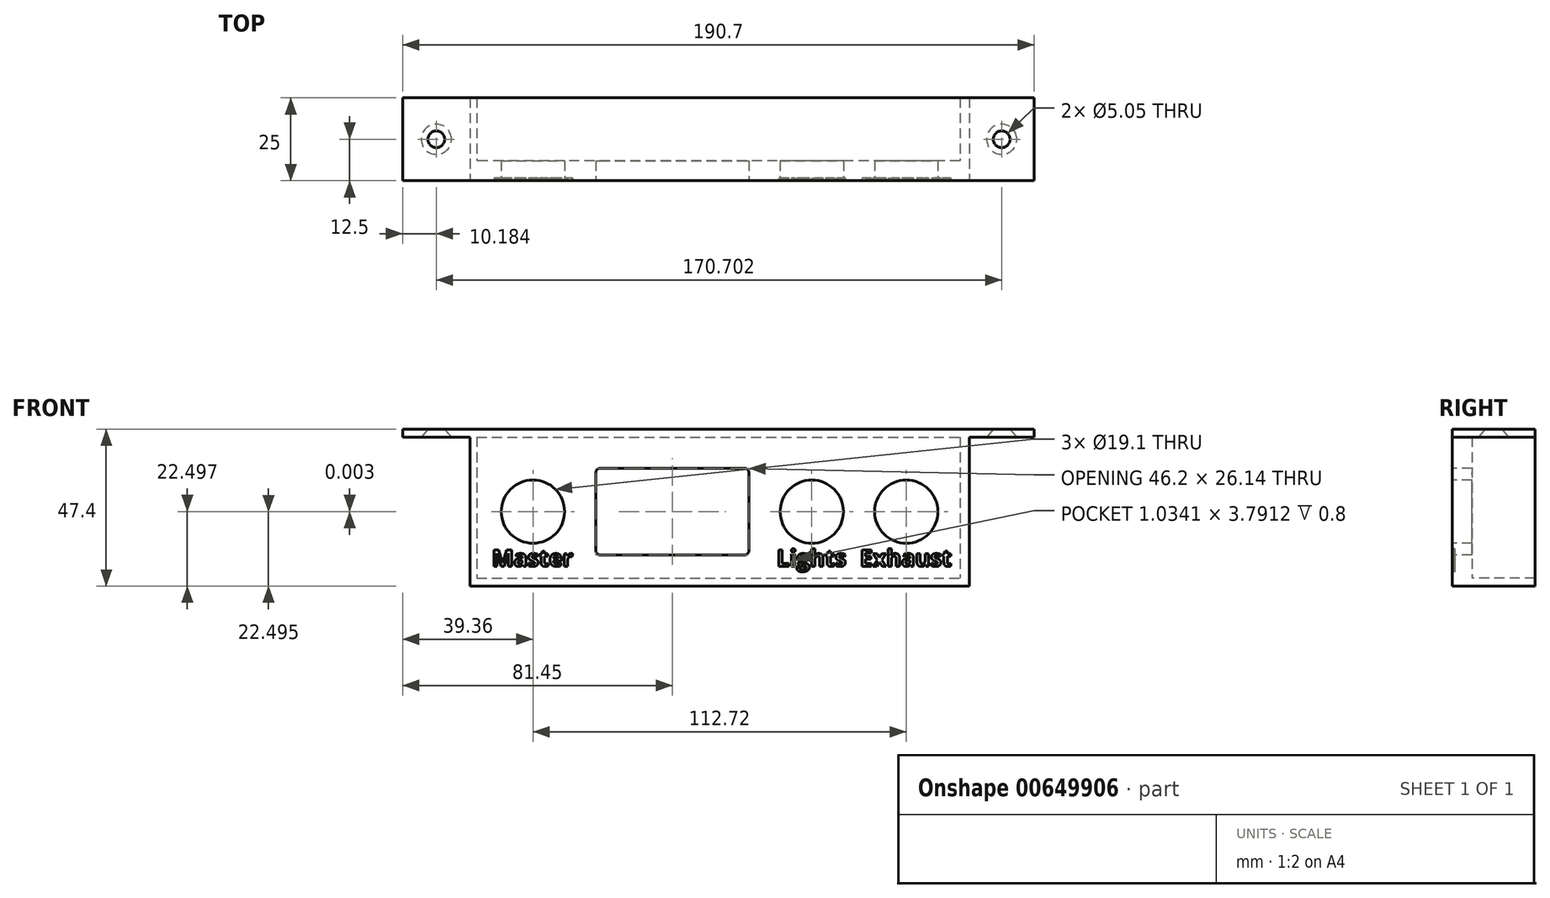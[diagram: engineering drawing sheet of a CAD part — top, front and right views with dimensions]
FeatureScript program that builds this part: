
annotation { "Feature Type Name" : "Feature", "Feature Type Description" : "" }
export const myFeature = defineFeature(function(context is Context, id is Id, definition is map)
    precondition{}
    {
        {
            var Q0;
            Q0=qCreatedBy(makeId("Front.planeOp"),FACE);
            var sketch = newSketch(context, id + "F0", { "sketchPlane" : qUnion([Q0])});
            skCircle(sketch, "E0", {"center": v(56.73, 0) * mm, "radius": 9.55 * mm});
            skCircle(sketch, "E1", {"center": v(28.2, 0) * mm, "radius": 9.55 * mm});
            skCircle(sketch, "E2", {"center": v(-55.99, 0) * mm, "radius": 9.55 * mm});
            skLineSegment(sketch, "E3.bottom", {"start": v(-35.73, -13.07) * mm, "end": v(7.93, -13.07) * mm});
            skLineSegment(sketch, "E3.top", {"start": v(-35.73, 13.07) * mm, "end": v(7.93, 13.07) * mm});
            skLineSegment(sketch, "E3.left", {"start": v(-37, -11.8) * mm, "end": v(-37, 11.8) * mm});
            skLineSegment(sketch, "E3.right", {"start": v(9.2, -11.8) * mm, "end": v(9.2, 11.8) * mm});
            skPoint(sketch, "E3.middle", {"position": v(-13.9, 0) * mm});
            skPoint(sketch, "E4.visualSharp", {"position": v(-37, -13.07) * mm});
            skArc(sketch, "E4.filletArc", {"start": v(-37, -11.8) * mm, "mid": v(-36.63, -12.7) * mm, "end": v(-35.73, -13.07) * mm});
            skPoint(sketch, "E5.visualSharp", {"position": v(9.2, -13.07) * mm});
            skArc(sketch, "E5.filletArc", {"start": v(7.93, -13.07) * mm, "mid": v(8.83, -12.7) * mm, "end": v(9.2, -11.8) * mm});
            skPoint(sketch, "E6.visualSharp", {"position": v(9.2, 13.07) * mm});
            skArc(sketch, "E6.filletArc", {"start": v(9.2, 11.8) * mm, "mid": v(8.83, 12.7) * mm, "end": v(7.93, 13.07) * mm});
            skPoint(sketch, "E7.visualSharp", {"position": v(-37, 13.07) * mm});
            skArc(sketch, "E7.filletArc", {"start": v(-35.73, 13.07) * mm, "mid": v(-36.63, 12.7) * mm, "end": v(-37, 11.8) * mm});
            skLineSegment(sketch, "E8.top", {"start": v(-74.98, -22.5) * mm, "end": v(75.72, -22.5) * mm});
            skLineSegment(sketch, "E8.left", {"start": v(-74.98, 22.5) * mm, "end": v(-74.98, -22.5) * mm});
            skLineSegment(sketch, "E8.right", {"start": v(75.72, 22.5) * mm, "end": v(75.72, -22.5) * mm});
            skPoint(sketch, "E9", {"position": v(0, 0) * mm});
            skLineSegment(sketch, "E10.bottom", {"start": v(-95.35, 24.9) * mm, "end": v(95.35, 24.9) * mm});
            skLineSegment(sketch, "E10.top", {"start": v(-95.35, 22.5) * mm, "end": v(-74.98, 22.5) * mm});
            skLineSegment(sketch, "E10.left", {"start": v(-95.35, 24.9) * mm, "end": v(-95.35, 22.5) * mm});
            skLineSegment(sketch, "E10.right", {"start": v(95.35, 24.9) * mm, "end": v(95.35, 22.5) * mm});
            skPoint(sketch, "E10.middle", {"position": v(0, 23.7) * mm});
            skLineSegment(sketch, "E11.trimOffspring", {"start": v(75.72, 22.5) * mm, "end": v(95.35, 22.5) * mm});
            skLineSegment(sketch, "E12.bottom", {"start": v(95.35, 22.5) * mm, "end": v(-95.35, 22.5) * mm});
            skLineSegment(sketch, "E12.top", {"start": v(95.35, 24.9) * mm, "end": v(-95.35, 24.9) * mm});
            skLineSegment(sketch, "E12.left", {"start": v(95.35, 22.5) * mm, "end": v(95.35, 24.9) * mm});
            skLineSegment(sketch, "E12.right", {"start": v(-95.35, 22.5) * mm, "end": v(-95.35, 24.9) * mm});
            skSolve(sketch);
        }
        {
            var Q0;
            Q0=makeQuery(id+"F0.imprint","IMPRINT",FACE,{"disambiguationData":[TD([[makeQuery(id+"F0.imprint","IMPRINT",EDGE,{"derivedFrom":sQuery(id+"F0.wireOp",EDGE,"E0")}),-1.0]])]});
            extrude(context, id + "F1", {"entities" : qUnion([Q0]), "oppositeDirection" : true, "depth" : 6 * mm, "offsetDistance" : 25 * mm});
        }
        {
            var Q0;
            Q0=makeQuery(id+"F0.imprint","IMPRINT",FACE,{"disambiguationData":[TD([[makeQuery(id+"F0.imprint","IMPRINT",EDGE,{"derivedFrom":sQuery(id+"F0.wireOp",EDGE,"E10.bottom")}),-1.0]])]});
            extrude(context, id + "F2", {"entities" : qUnion([Q0]), "operationType" : NewBodyOperationType.ADD, "oppositeDirection" : true, "depth" : 25 * mm, "offsetDistance" : 25 * mm});
        }
        {
            var Q0;
            Q0=qCreatedBy(makeId("Front.planeOp"),FACE);
            var sketch = newSketch(context, id + "F3", { "sketchPlane" : qUnion([Q0])});
            skLineSegment(sketch, "E13.0", {"start": v(-74.98, -22.5) * mm, "end": v(75.72, -22.5) * mm});
            skLineSegment(sketch, "E13.1", {"start": v(75.72, 22.5) * mm, "end": v(75.72, -22.5) * mm});
            skLineSegment(sketch, "E13.2", {"start": v(-74.98, 22.5) * mm, "end": v(-74.98, -22.5) * mm});
            skLineSegment(sketch, "E13.3", {"start": v(95.35, 22.5) * mm, "end": v(72.95, 22.5) * mm});
            skLineSegment(sketch, "E14.left", {"start": v(72.95, 20.1) * mm, "end": v(72.95, -20.1) * mm});
            skLineSegment(sketch, "E14.right", {"start": v(-72.95, 20.1) * mm, "end": v(-72.95, -20.1) * mm});
            skPoint(sketch, "E14.middle", {"position": v(0, 0) * mm});
            skLineSegment(sketch, "E15", {"start": v(-72.95, 22.5) * mm, "end": v(-72.95, -20.1) * mm});
            skLineSegment(sketch, "E16", {"start": v(72.95, 22.5) * mm, "end": v(72.95, -20.1) * mm});
            skLineSegment(sketch, "E17", {"start": v(-72.95, -20.1) * mm, "end": v(72.95, -20.1) * mm});
            skLineSegment(sketch, "E18.trimOffspring", {"start": v(-72.95, 22.5) * mm, "end": v(-95.35, 22.5) * mm});
            skSolve(sketch);
        }
        {
            var Q0;
            Q0=makeQuery(id+"F3.imprint","IMPRINT",FACE,{"disambiguationData":[TD([[makeQuery(id+"F3.imprint","IMPRINT",EDGE,{"derivedFrom":sQuery(id+"F3.wireOp",EDGE,"E13.0")}),1.0]])]});
            extrude(context, id + "F4", {"entities" : qUnion([Q0]), "operationType" : NewBodyOperationType.ADD, "oppositeDirection" : true, "depth" : 25 * mm, "offsetDistance" : 25 * mm});
        }
        {
            var Q0;
            {var subQ0=sQuery(id+"F0.wireOp",EDGE,"E12.bottom");var subQ1=sQuery(id+"F0.wireOp",EDGE,"E11.trimOffspring");var subQ4=sQuery(id+"F0.wireOp",EDGE,"E10.top");var subQ6=sQuery(id+"F0.wireOp",EDGE,"E8.right");Q0=makeQuery(id+"F4.boolean.opBoolean","SPLIT",FACE,{"disambiguationData":[TD([makeQuery(id+"F1.opExtrude","SWEPT_FACE",FACE,{"disambiguationData":[OSD([subQ6])]})])],"derivedFrom":makeQuery(id+"F2.opExtrude","SWEPT_FACE",FACE,{"disambiguationData":[OSD([subQ4,subQ1,subQ0])]})});}
            var sketch = newSketch(context, id + "F5", { "sketchPlane" : qUnion([Q0])});
            skLineSegment(sketch, "E19.0.0", {"start": v(75.72, 0) * mm, "end": v(75.72, -25) * mm});
            skLineSegment(sketch, "E19.0.1", {"start": v(75.72, -25) * mm, "end": v(95.35, -25) * mm});
            skLineSegment(sketch, "E19.0.2", {"start": v(95.35, -25) * mm, "end": v(95.35, 0) * mm});
            skLineSegment(sketch, "E19.0.3", {"start": v(95.35, 0) * mm, "end": v(75.72, 0) * mm});
            skLineSegment(sketch, "E20.0.0", {"start": v(-95.35, -25) * mm, "end": v(-74.98, -25) * mm});
            skLineSegment(sketch, "E20.0.1", {"start": v(-74.98, -25) * mm, "end": v(-74.98, 0) * mm});
            skLineSegment(sketch, "E20.0.2", {"start": v(-74.98, 0) * mm, "end": v(-95.35, 0) * mm});
            skLineSegment(sketch, "E20.0.3", {"start": v(-95.35, 0) * mm, "end": v(-95.35, -25) * mm});
            skPoint(sketch, "E21", {"position": v(85.54, -12.5) * mm});
            skPoint(sketch, "E21.positionSnap0", {"position": v(95.35, -12.5) * mm});
            skPoint(sketch, "E21.positionSnap1", {"position": v(85.54, -25) * mm});
            skPoint(sketch, "E22", {"position": v(-85.17, -12.5) * mm});
            skPoint(sketch, "E22.positionSnap0", {"position": v(-85.17, -25) * mm});
            skPoint(sketch, "E22.positionSnap1", {"position": v(-95.35, -12.5) * mm});
            skSolve(sketch);
        }
        {
            var Q0;
            Q0=sQuery(id+"F5.wireOp",VERTEX,"E21");
            var Q1;
            Q1=sQuery(id+"F5.wireOp",VERTEX,"E22");
            var Q2;
            Q2=makeQuery(id+"F1.opExtrude","SWEPT_BODY",BODY,{"disambiguationData":[OSD([sQuery(id+"F0.wireOp",EDGE,"E0"),sQuery(id+"F0.wireOp",EDGE,"E1"),sQuery(id+"F0.wireOp",EDGE,"E2"),sQuery(id+"F0.wireOp",EDGE,"E3.bottom"),sQuery(id+"F0.wireOp",EDGE,"E3.top"),sQuery(id+"F0.wireOp",EDGE,"E3.left"),sQuery(id+"F0.wireOp",EDGE,"E3.right"),sQuery(id+"F0.wireOp",EDGE,"E4.filletArc"),sQuery(id+"F0.wireOp",EDGE,"E5.filletArc"),sQuery(id+"F0.wireOp",EDGE,"E6.filletArc"),sQuery(id+"F0.wireOp",EDGE,"E7.filletArc"),sQuery(id+"F0.wireOp",EDGE,"E8.top"),sQuery(id+"F0.wireOp",EDGE,"E8.left"),sQuery(id+"F0.wireOp",EDGE,"E8.right"),sQuery(id+"F0.wireOp",EDGE,"E12.bottom")])]});
            hole(context, id + "F6", {"style" : HoleStyle.C_SINK, "endStyle" : HoleEndStyle.THROUGH, "standardTappedOrClearance" : lookupTablePath({ "standard" : "ANSI", "size" : "#8 (0.2)", "type" : "Drilled" }), "standardBlindInLast" : lookupTablePath({ "standard" : "ANSI", "size" : "#8", "type" : "Drilled" }), "holeDiameter" : 5.05 * mm, "cSinkDiameter" : 9.12 * mm, "cSinkAngle" : 82 * degree, "majorDiameter" : 4.17 * mm, "isTappedThrough" : true, "tappedDepth" : 12 * mm, "tapClearance" : 3, "locations" : qUnion([Q0, Q1]), "scope" : qUnion([Q2])});
        }
        {
            var Q0;
            {var subQ0=sQuery(id+"F0.wireOp",EDGE,"E12.bottom");Q0=makeQuery(id+"F2.boolean.opBoolean","MERGE",FACE,{"derivedFrom":[makeQuery(id+"F1.opExtrude","CAP_FACE",FACE,{"disambiguationData":[OSD([sQuery(id+"F0.wireOp",EDGE,"E0"),sQuery(id+"F0.wireOp",EDGE,"E1"),sQuery(id+"F0.wireOp",EDGE,"E2"),sQuery(id+"F0.wireOp",EDGE,"E3.bottom"),sQuery(id+"F0.wireOp",EDGE,"E3.top"),sQuery(id+"F0.wireOp",EDGE,"E3.left"),sQuery(id+"F0.wireOp",EDGE,"E3.right"),sQuery(id+"F0.wireOp",EDGE,"E4.filletArc"),sQuery(id+"F0.wireOp",EDGE,"E5.filletArc"),sQuery(id+"F0.wireOp",EDGE,"E6.filletArc"),sQuery(id+"F0.wireOp",EDGE,"E7.filletArc"),sQuery(id+"F0.wireOp",EDGE,"E8.top"),sQuery(id+"F0.wireOp",EDGE,"E8.left"),sQuery(id+"F0.wireOp",EDGE,"E8.right"),subQ0])],"isStart":true}),makeQuery(id+"F2.opExtrude","CAP_FACE",FACE,{"disambiguationData":[OSD([sQuery(id+"F0.wireOp",EDGE,"E10.bottom"),sQuery(id+"F0.wireOp",EDGE,"E10.top"),sQuery(id+"F0.wireOp",EDGE,"E10.left"),sQuery(id+"F0.wireOp",EDGE,"E10.right"),sQuery(id+"F0.wireOp",EDGE,"E11.trimOffspring"),subQ0])],"isStart":true})]});}
            var sketch = newSketch(context, id + "F7", { "sketchPlane" : qUnion([Q0])});
            skLineSegment(sketch, "E23", {"start": v(74.98, -11.5) * mm, "end": v(74.98, -17.5) * mm});
            skText(sketch, "E24", { "text": "Exhaust", "fontName": "OpenSans-Bold.ttf"});
            skText(sketch, "E25", { "text": "Lights", "fontName": "OpenSans-Bold.ttf"});
            skText(sketch, "E26", { "text": "Master", "fontName": "OpenSans-Bold.ttf"});
            const initialGuessF7  = {"E24": [0.04274, -0.0165, 1, 0, 0.005], "E25": [0.01761, -0.0165, 1, 0, 0.005], "E26": [-0.06838, -0.0165, 1, 0, 0.005]};
            skSetInitialGuess(sketch, initialGuessF7);
            skSolve(sketch);
        }
        {
            var Q0;
            Q0 = qSketchRegion(id + "F7", true);
            extrude(context, id + "F8", {"entities" : qUnion([Q0]), "operationType" : NewBodyOperationType.REMOVE, "oppositeDirection" : true, "depth" : .8 * mm, "offsetDistance" : 25 * mm});
        }
    });
